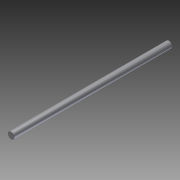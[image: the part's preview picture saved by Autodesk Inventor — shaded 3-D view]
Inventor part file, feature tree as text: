
AUTODESK INVENTOR PART (.ipt)
format: ipt  version: 2012 (Build 160160000, 160)  size: 64,512 bytes
history: native  units: in
note: dims shown in document units (in); Inventor stores cm internally (conversion verified against a paired STEP export)
features: extrude x1, sketch x1
ambient origin geometry x8: Origin, YZ Plane, XZ Plane, XY Plane, X Axis, Y Axis, Z Axis, Center Point
bodies: Solid1 (feature_tree)
feature tree (2):
  extrude  "Extrusion1"  Depth=12.0in TaperAngle=0.0deg
  sketch  "Sketch1"  dims[d0=0.5in d1=12.0in d2=0.0in]
